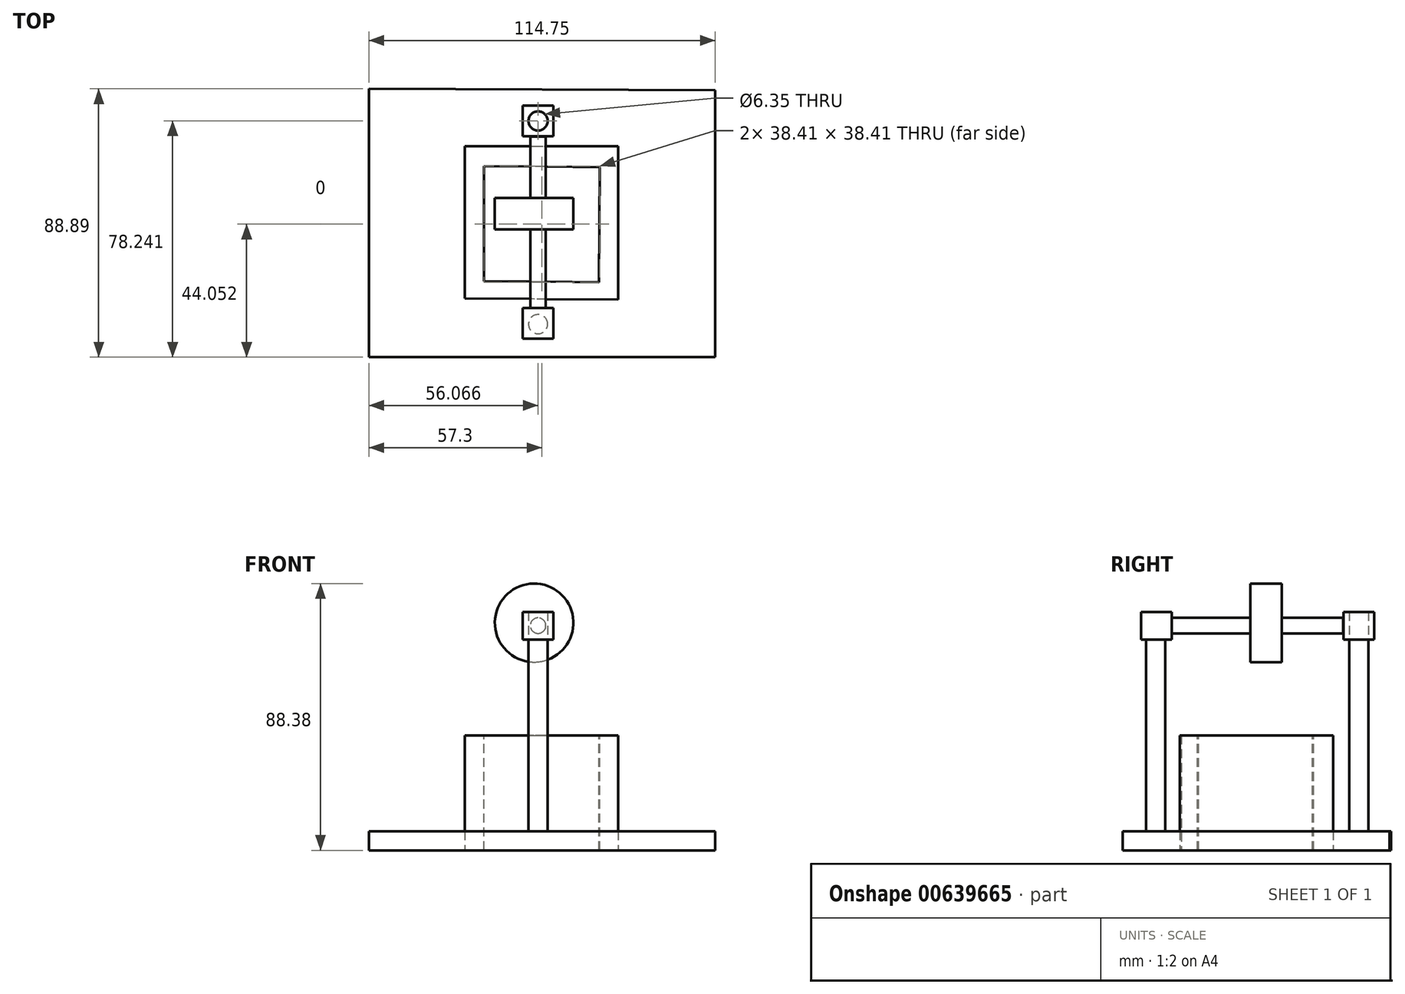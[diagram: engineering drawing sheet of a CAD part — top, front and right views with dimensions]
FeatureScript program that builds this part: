
annotation { "Feature Type Name" : "Feature", "Feature Type Description" : "" }
export const myFeature = defineFeature(function(context is Context, id is Id, definition is map)
    precondition{}
    {
        {
            var Q0;
            Q0=qCreatedBy(makeId("Top.planeOp"),FACE);
            var sketch = newSketch(context, id + "F0", { "sketchPlane" : qUnion([Q0])});
            skLineSegment(sketch, "E0", {"start": v(-106.05, 75.8) * mm, "end": v(-106.05, -25.8) * mm});
            skLineSegment(sketch, "E1", {"start": v(-106.05, -25.8) * mm, "end": v(20.95, -25.8) * mm});
            skLineSegment(sketch, "E2", {"start": v(20.95, -25.8) * mm, "end": v(20.95, 75.8) * mm});
            skLineSegment(sketch, "E3", {"start": v(20.95, 75.8) * mm, "end": v(-106.05, 75.8) * mm});
            skPoint(sketch, "E4.endSnap0", {"position": v(-42.55, 75.8) * mm});
            skLineSegment(sketch, "E5", {"start": v(-42.55, 50.4) * mm, "end": v(-17.15, 50.4) * mm});
            skLineSegment(sketch, "E6", {"start": v(-17.15, 50.4) * mm, "end": v(-17.15, -0.4) * mm});
            skLineSegment(sketch, "E7", {"start": v(-17.15, -0.4) * mm, "end": v(-67.94, 0) * mm});
            skLineSegment(sketch, "E8", {"start": v(-67.94, 0) * mm, "end": v(-67.94, 50.4) * mm});
            skLineSegment(sketch, "E9", {"start": v(-67.94, 50.4) * mm, "end": v(-42.55, 50.4) * mm});
            skLineSegment(sketch, "E10", {"start": v(14.6, 69.44) * mm, "end": v(14.6, -19.46) * mm});
            skLineSegment(sketch, "E11", {"start": v(-99.7, 69.44) * mm, "end": v(14.6, 69.44) * mm});
            skLineSegment(sketch, "E12", {"start": v(-99.7, -19.46) * mm, "end": v(14.6, -19.46) * mm});
            skLineSegment(sketch, "E13", {"start": v(-99.7, -19.46) * mm, "end": v(-99.7, 69.44) * mm});
            skSolve(sketch);
        }
        {
            var Q0;
            Q0=makeQuery(id+"F0.imprint","IMPRINT",FACE,{"disambiguationData":[TD([[makeQuery(id+"F0.imprint","IMPRINT",EDGE,{"derivedFrom":sQuery(id+"F0.wireOp",EDGE,"E5")}),-1.0]])]});
            extrude(context, id + "F1", {"entities" : qUnion([Q0]), "depth" : 38.1 * mm, "offsetDistance" : 25.4 * mm});
        }
        {
            var Q0;
            Q0=qCreatedBy(makeId("Top.planeOp"),FACE);
            var sketch = newSketch(context, id + "F2", { "sketchPlane" : qUnion([Q0])});
            skLineSegment(sketch, "E14", {"start": v(-99.7, 69.45) * mm, "end": v(-99.7, -19.44) * mm});
            skLineSegment(sketch, "E15", {"start": v(-99.7, -19.44) * mm, "end": v(15.06, -19.44) * mm});
            skLineSegment(sketch, "E16", {"start": v(15.06, -19.44) * mm, "end": v(15.06, 68.95) * mm});
            skLineSegment(sketch, "E17", {"start": v(15.06, 68.95) * mm, "end": v(-99.7, 69.45) * mm});
            skSolve(sketch);
        }
        {
            var Q0;
            Q0=makeQuery(id+"F2.imprint","IMPRINT",FACE,{"disambiguationData":[TD([[makeQuery(id+"F2.imprint","IMPRINT",EDGE,{"derivedFrom":sQuery(id+"F2.wireOp",EDGE,"E14")}),1.0]])]});
            extrude(context, id + "F3", {"entities" : qUnion([Q0]), "depth" : 6.35 * mm, "offsetDistance" : 25.4 * mm});
        }
        {
            var Q0;
            Q0=makeQuery(id+"F1.opExtrude","CAP_FACE",FACE,{"disambiguationData":[OSD([sQuery(id+"F0.wireOp",EDGE,"E5"),sQuery(id+"F0.wireOp",EDGE,"E6"),sQuery(id+"F0.wireOp",EDGE,"E7"),sQuery(id+"F0.wireOp",EDGE,"E8"),sQuery(id+"F0.wireOp",EDGE,"E9")])],"isStart":false});
            var sketch = newSketch(context, id + "F4", { "sketchPlane" : qUnion([Q0])});
            skLineSegment(sketch, "E18", {"start": v(-61.6, 5.72) * mm, "end": v(-23.5, 5.4) * mm});
            skLineSegment(sketch, "E19", {"start": v(-23.5, 5.4) * mm, "end": v(-23.19, 43.5) * mm});
            skLineSegment(sketch, "E20", {"start": v(-23.19, 43.5) * mm, "end": v(-61.6, 43.82) * mm});
            skLineSegment(sketch, "E21", {"start": v(-61.6, 43.82) * mm, "end": v(-61.6, 5.72) * mm});
            skSolve(sketch);
        }
        {
            var Q0;
            Q0=makeQuery(id+"F4.imprint","IMPRINT",FACE,{"disambiguationData":[TD([[makeQuery(id+"F4.imprint","IMPRINT",EDGE,{"derivedFrom":sQuery(id+"F4.wireOp",EDGE,"E18")}),1.0]])]});
            extrude(context, id + "F5", {"entities" : qUnion([Q0]), "operationType" : NewBodyOperationType.REMOVE, "oppositeDirection" : true, "depth" : 111.76 * mm, "offsetDistance" : 25.4 * mm});
        }
        {
            var Q0;
            Q0=makeQuery(id+"F3.opExtrude","CAP_FACE",FACE,{"disambiguationData":[OSD([sQuery(id+"F2.wireOp",EDGE,"E14"),sQuery(id+"F2.wireOp",EDGE,"E15"),sQuery(id+"F2.wireOp",EDGE,"E16"),sQuery(id+"F2.wireOp",EDGE,"E17")])],"isStart":false});
            var sketch = newSketch(context, id + "F6", { "sketchPlane" : qUnion([Q0])});
            skCircle(sketch, "E22", {"center": v(-43.62, -8.5) * mm, "radius": 3.18 * mm});
            skCircle(sketch, "E23", {"center": v(-43.62, 58.8) * mm, "radius": 3.18 * mm});
            skSolve(sketch);
        }
        {
            var Q0;
            Q0=makeQuery(id+"F6.imprint","IMPRINT",FACE,{"disambiguationData":[TD([[makeQuery(id+"F6.imprint","IMPRINT",EDGE,{"derivedFrom":sQuery(id+"F6.wireOp",EDGE,"E23")}),1.0]])]});
            var Q1;
            Q1=makeQuery(id+"F6.imprint","IMPRINT",FACE,{"disambiguationData":[TD([[makeQuery(id+"F6.imprint","IMPRINT",EDGE,{"derivedFrom":sQuery(id+"F6.wireOp",EDGE,"E22")}),1.0]])]});
            extrude(context, id + "F7", {"entities" : qUnion([Q0, Q1]), "operationType" : NewBodyOperationType.ADD, "depth" : 63.5 * mm, "offsetDistance" : 25.4 * mm});
        }
        {
            var Q0;
            Q0=makeQuery(id+"F7.opExtrude","CAP_FACE",FACE,{"disambiguationData":[OSD([sQuery(id+"F6.wireOp",EDGE,"E23")])],"isStart":false});
            var sketch = newSketch(context, id + "F8", { "sketchPlane" : qUnion([Q0])});
            skLineSegment(sketch, "E24", {"start": v(-48.7, 59.82) * mm, "end": v(-48.7, 63.88) * mm});
            skLineSegment(sketch, "E25", {"start": v(-48.7, 63.88) * mm, "end": v(-38.54, 63.88) * mm});
            skLineSegment(sketch, "E26", {"start": v(-38.54, 63.88) * mm, "end": v(-38.54, 53.72) * mm});
            skLineSegment(sketch, "E27", {"start": v(-38.54, 53.72) * mm, "end": v(-48.7, 53.72) * mm});
            skLineSegment(sketch, "E28", {"start": v(-48.7, 53.72) * mm, "end": v(-48.7, 63.88) * mm});
            skLineSegment(sketch, "E29", {"start": v(-48.7, -7.5) * mm, "end": v(-48.7, -3.18) * mm});
            skLineSegment(sketch, "E30", {"start": v(-48.7, -3.18) * mm, "end": v(-38.54, -3.18) * mm});
            skLineSegment(sketch, "E31", {"start": v(-38.54, -3.18) * mm, "end": v(-38.54, -13.34) * mm});
            skLineSegment(sketch, "E32", {"start": v(-38.54, -13.34) * mm, "end": v(-48.7, -13.34) * mm});
            skLineSegment(sketch, "E33", {"start": v(-48.7, -13.34) * mm, "end": v(-48.7, -3.18) * mm});
            skSolve(sketch);
        }
        {
            var Q0;
            {var subQ3=sQuery(id+"F8.wireOp",EDGE,"E25");Q0=makeQuery(id+"F8.imprint","IMPRINT",FACE,{"disambiguationData":[TD([[makeQuery(id+"F8.imprint","IMPRINT",EDGE,{"derivedFrom":subQ3}),-1.0]])]});}
            var Q1;
            {var subQ3=sQuery(id+"F8.wireOp",EDGE,"E30");Q1=makeQuery(id+"F8.imprint","IMPRINT",FACE,{"disambiguationData":[TD([[makeQuery(id+"F8.imprint","IMPRINT",EDGE,{"derivedFrom":subQ3}),-1.0]])]});}
            extrude(context, id + "F9", {"entities" : qUnion([Q0, Q1]), "operationType" : NewBodyOperationType.ADD, "depth" : 9.14 * mm, "offsetDistance" : 25.4 * mm});
        }
        {
            var Q0;
            Q0=makeQuery(id+"F9.opExtrude","SWEPT_FACE",FACE,{"disambiguationData":[OSD([sQuery(id+"F8.wireOp",EDGE,"E30")])]});
            var sketch = newSketch(context, id + "F10", { "sketchPlane" : qUnion([Q0])});
            skCircle(sketch, "E34", {"center": v(43.62, 74.42) * mm, "radius": 2.58 * mm});
            skPoint(sketch, "E34.centerSnap0", {"position": v(43.62, 69.85) * mm});
            skPoint(sketch, "E34.centerSnap1", {"position": v(38.54, 74.42) * mm});
            skSolve(sketch);
        }
        {
            var Q0;
            Q0=makeQuery(id+"F10.imprint","IMPRINT",FACE,{"disambiguationData":[TD([[makeQuery(id+"F10.imprint","IMPRINT",EDGE,{"derivedFrom":sQuery(id+"F10.wireOp",EDGE,"E34")}),1.0]])]});
            extrude(context, id + "F11", {"entities" : qUnion([Q0]), "operationType" : NewBodyOperationType.ADD, "depth" : 56.8 * mm, "offsetDistance" : 25.4 * mm});
        }
        {
            var Q0;
            Q0=qCreatedBy(makeId("Front.planeOp"),FACE);
            var sketch = newSketch(context, id + "F12", { "sketchPlane" : qUnion([Q0])});
            skCircle(sketch, "E35", {"center": v(-44.93, 75.36) * mm, "radius": 13.01 * mm});
            skSolve(sketch);
        }
        {
            var Q0;
            Q0=makeQuery(id+"F12.imprint","IMPRINT",FACE,{"disambiguationData":[TD([[makeQuery(id+"F12.imprint","IMPRINT",EDGE,{"derivedFrom":sQuery(id+"F12.wireOp",EDGE,"E35")}),1.0]])]});
            extrude(context, id + "F13", {"entities" : qUnion([Q0]), "operationType" : NewBodyOperationType.ADD, "oppositeDirection" : true, "depth" : 33.27 * mm, "offsetDistance" : 25.4 * mm});
        }
        {
            var Q0;
            Q0=makeQuery(id+"F13.opExtrude","CAP_FACE",FACE,{"disambiguationData":[OSD([sQuery(id+"F12.wireOp",EDGE,"E35")])],"isStart":true});
            extrude(context, id + "F14", {"entities" : qUnion([Q0]), "operationType" : NewBodyOperationType.REMOVE, "oppositeDirection" : true, "depth" : 22.86 * mm, "offsetDistance" : 25.4 * mm});
        }
    });
